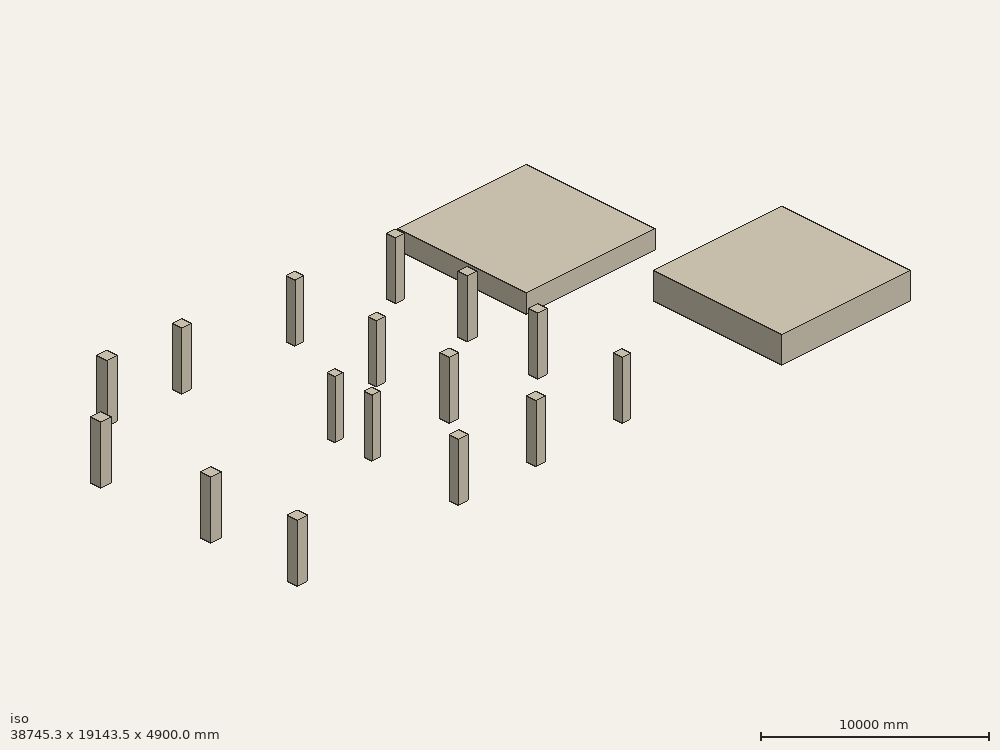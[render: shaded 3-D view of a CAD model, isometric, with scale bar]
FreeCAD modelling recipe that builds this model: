
FCSTD DOCUMENT  (FreeCAD 0.19R24291 (Git))
Label: single_foundation
License: All rights reserved
LicenseURL: http://en.wikipedia.org/wiki/All_rights_reserved
objects: Part::Part2DObjectPython×68, Part::FeaturePython×55, App::FeaturePython×17, App::DocumentObjectGroup×5
note: 280 computed .brp shape members not serialized (recipe doc carries the construction recipe); baked Part::Feature solids carry a one-line shape summary decoded from their .brp

FEATURE [Part::Part2DObjectPython] Line006  label="C1_Story1_CenterLine"  # Draft 2D object (typed FeaturePython)
  Area = 0
  ChamferSize = 0
  Closed = false
  End = (17740,20340,3350)
  FilletRadius = 0
  Length = 3350
  MakeFace = true
  Points = (2) [(17740,20340,0),(17740,20340,3350)]
  Start = (17740,20340,0)
  Subdivisions = 0
FEATURE [Part::Part2DObjectPython] C5512C  # Draft 2D object (typed FeaturePython)
  Height = 550
  Width = 550
FEATURE [Part::FeaturePython] Structure  label="C1_Story1"  # Arch/BIM 24 (typed FeaturePython)
  AttacherType = Attacher::AttachEngine3D
  AttachmentOffset = pos=(0,0,0) rot=(0,0,1;1.5708rad)
  Base = -> C5512C
  FaceMaker = 0
  Height = 3350
  HorizontalArea = 302500
  IfcData = attributes={"GlobalId": {"name": "GlobalId", "type": "IfcGloballyUniqueId", "is_enum": false, "enum_values": []}, "Description": {"... (+438 chars omitted),+1 more (map truncated)
  IfcType = 24
  Length = 0
  MapMode = 7
  MoveBase = false
  MoveWithHost = false
  Nodes = (2) [(17740,20340,0),(17740,20340,3350)]
  NodesOffset = 0
  Normal = (0,0,0)
  PerimeterLength = 2200
  Placement = pos=(17740,20340,0) rot=(0,0,1;1.5708rad)
  PredefinedType = 0
  Support = -> [Line006]
  VerticalArea = 7.37e+06
  Width = 200
  combos_load = Combo1 Max=2929.3594, 27006.37, 14808.13,Combo10 Max=2608.538, -98112.68, -391082.9,Combo11 Max=2657.75, -72288.26, -345375.92,+37 more (map truncated)
FEATURE [Part::Part2DObjectPython] Line007  label="C2_Story1_CenterLine"  # Draft 2D object (typed FeaturePython)
  Area = 0
  ChamferSize = 0
  Closed = false
  End = (23500,19838.5,3350)
  FilletRadius = 0
  Length = 3350
  MakeFace = true
  Points = (2) [(23500,19838.5,0),(23500,19838.5,3350)]
  Start = (23500,19838.5,0)
  Subdivisions = 0
FEATURE [Part::FeaturePython] Structure001  label="C2_Story1"  # Arch/BIM 24 (typed FeaturePython)
  AttacherType = Attacher::AttachEngine3D
  AttachmentOffset = pos=(0,0,0) rot=(0,0,1;1.5708rad)
  Base = -> C5512C
  FaceMaker = 0
  Height = 3350
  HorizontalArea = 302500
  IfcData = attributes={"GlobalId": {"name": "GlobalId", "type": "IfcGloballyUniqueId", "is_enum": false, "enum_values": []}, "Description": {"... (+438 chars omitted),+1 more (map truncated)
  IfcType = 24
  Length = 0
  MapMode = 7
  MoveBase = false
  MoveWithHost = false
  Nodes = (2) [(23500,19838.5,0),(23500,19838.5,3350)]
  NodesOffset = 0
  Normal = (0,0,0)
  PerimeterLength = 2200
  Placement = pos=(23500,19838.5,0) rot=(0,0,1;1.5708rad)
  PredefinedType = 0
  Support = -> [Line007]
  VerticalArea = 7.37e+06
  Width = 200
  combos_load = Combo1 Max=1754.8461, 12356.17, -26849.18,Combo10 Max=2143.525, -139905.36, -387343.42,Combo11 Max=2175.8338, -83310.12, -350318.73,+37 more (map truncated)
FEATURE [Part::Part2DObjectPython] Line008  label="C17_Story1_CenterLine"  # Draft 2D object (typed FeaturePython)
  Area = 0
  ChamferSize = 0
  Closed = false
  End = (23370,15250,3350)
  FilletRadius = 0
  Length = 3350
  MakeFace = true
  Points = (2) [(23370,15250,0),(23370,15250,3350)]
  Start = (23370,15250,0)
  Subdivisions = 0
FEATURE [Part::Part2DObjectPython] C6012AC  # Draft 2D object (typed FeaturePython)
  Height = 600
  Width = 600
FEATURE [Part::FeaturePython] Structure002  label="C17_Story1"  # Arch/BIM 24 (typed FeaturePython)
  AttacherType = Attacher::AttachEngine3D
  AttachmentOffset = pos=(0,0,0) rot=(0,0,1;1.5708rad)
  Base = -> C6012AC
  FaceMaker = 0
  Height = 3350
  HorizontalArea = 360000
  IfcData = attributes={"GlobalId": {"name": "GlobalId", "type": "IfcGloballyUniqueId", "is_enum": false, "enum_values": []}, "Description": {"... (+438 chars omitted),+1 more (map truncated)
  IfcType = 24
  Length = 0
  MapMode = 7
  MoveBase = false
  MoveWithHost = false
  Nodes = (2) [(23370,15250,0),(23370,15250,3350)]
  NodesOffset = 0
  Normal = (0,0,0)
  PerimeterLength = 2400
  Placement = pos=(23370,15250,0) rot=(0,0,1;1.5708rad)
  PredefinedType = 0
  Support = -> [Line008]
  VerticalArea = 8.04e+06
  Width = 200
  combos_load = Combo1 Max=1514.2218, -5536.02, -34563.49,Combo10 Max=1873.5598, -222983.25, -488160.13,Combo11 Max=1871.0673, -140666.82, -475481.05,+37 more (map truncated)
FEATURE [Part::Part2DObjectPython] Line009  label="C18_Story1_CenterLine"  # Draft 2D object (typed FeaturePython)
  Area = 0
  ChamferSize = 0
  Closed = false
  End = (23250,10750,3350)
  FilletRadius = 0
  Length = 3350
  MakeFace = true
  Points = (2) [(23250,10750,0),(23250,10750,3350)]
  Start = (23250,10750,0)
  Subdivisions = 0
FEATURE [Part::FeaturePython] Structure003  label="C18_Story1"  # Arch/BIM 24 (typed FeaturePython)
  AttacherType = Attacher::AttachEngine3D
  AttachmentOffset = pos=(0,0,0) rot=(0,0,1;1.5708rad)
  Base = -> C6012AC
  FaceMaker = 0
  Height = 3350
  HorizontalArea = 360000
  IfcData = attributes={"GlobalId": {"name": "GlobalId", "type": "IfcGloballyUniqueId", "is_enum": false, "enum_values": []}, "Description": {"... (+438 chars omitted),+1 more (map truncated)
  IfcType = 24
  Length = 0
  MapMode = 7
  MoveBase = false
  MoveWithHost = false
  Nodes = (2) [(23250,10750,0),(23250,10750,3350)]
  NodesOffset = 0
  Normal = (0,0,0)
  PerimeterLength = 2400
  Placement = pos=(23250,10750,0) rot=(0,0,1;1.5708rad)
  PredefinedType = 0
  Support = -> [Line009]
  VerticalArea = 8.04e+06
  Width = 200
  combos_load = Combo1 Max=1534.3408, 49.31, -39260.22,Combo10 Max=2051.3394, -213536.56, -457180.36,Combo11 Max=2057.4036, -133173.75, -478456.04,+37 more (map truncated)
FEATURE [Part::Part2DObjectPython] Line010  label="C5_Story1_CenterLine"  # Draft 2D object (typed FeaturePython)
  Area = 0
  ChamferSize = 0
  Closed = false
  End = (17740,5350,3350)
  FilletRadius = 0
  Length = 3350
  MakeFace = true
  Points = (2) [(17740,5350,0),(17740,5350,3350)]
  Start = (17740,5350,0)
  Subdivisions = 0
FEATURE [Part::FeaturePython] Structure004  label="C5_Story1"  # Arch/BIM 24 (typed FeaturePython)
  AttacherType = Attacher::AttachEngine3D
  AttachmentOffset = pos=(0,0,0) rot=(0,0,1;1.5708rad)
  Base = -> C6012AC
  FaceMaker = 0
  Height = 3350
  HorizontalArea = 360000
  IfcData = attributes={"GlobalId": {"name": "GlobalId", "type": "IfcGloballyUniqueId", "is_enum": false, "enum_values": []}, "Description": {"... (+438 chars omitted),+1 more (map truncated)
  IfcType = 24
  Length = 0
  MapMode = 7
  MoveBase = false
  MoveWithHost = false
  Nodes = (2) [(17740,5350,0),(17740,5350,3350)]
  NodesOffset = 0
  Normal = (0,0,0)
  PerimeterLength = 2400
  Placement = pos=(17740,5350,0) rot=(0,0,1;1.5708rad)
  PredefinedType = 0
  Support = -> [Line010]
  VerticalArea = 8.04e+06
  Width = 200
  combos_load = Combo1 Max=1623.3033, -947.79, -5177.17,Combo10 Max=1786.5067, -169313.57, -460450.33,Combo11 Max=1770.754, -135335.23, -531760.45,+37 more (map truncated)
FEATURE [Part::Part2DObjectPython] Line011  label="C6_Story1_CenterLine"  # Draft 2D object (typed FeaturePython)
  Area = 0
  ChamferSize = 0
  Closed = false
  End = (12940,5350,3350)
  FilletRadius = 0
  Length = 3350
  MakeFace = true
  Points = (2) [(12940,5350,0),(12940,5350,3350)]
  Start = (12940,5350,0)
  Subdivisions = 0
FEATURE [Part::FeaturePython] Structure005  label="C6_Story1"  # Arch/BIM 24 (typed FeaturePython)
  AttacherType = Attacher::AttachEngine3D
  AttachmentOffset = pos=(0,0,0) rot=(0,0,1;1.5708rad)
  Base = -> C6012AC
  FaceMaker = 0
  Height = 3350
  HorizontalArea = 360000
  IfcData = attributes={"GlobalId": {"name": "GlobalId", "type": "IfcGloballyUniqueId", "is_enum": false, "enum_values": []}, "Description": {"... (+438 chars omitted),+1 more (map truncated)
  IfcType = 24
  Length = 0
  MapMode = 7
  MoveBase = false
  MoveWithHost = false
  Nodes = (2) [(12940,5350,0),(12940,5350,3350)]
  NodesOffset = 0
  Normal = (0,0,0)
  PerimeterLength = 2400
  Placement = pos=(12940,5350,0) rot=(0,0,1;1.5708rad)
  PredefinedType = 0
  Support = -> [Line011]
  VerticalArea = 8.04e+06
  Width = 200
  combos_load = Combo1 Max=2458.9073, 10889.53, -106700.8,Combo10 Max=1939.8727, -132976.26, -554878.34,Combo11 Max=1860.3718, -132910.34, -622641.45,+37 more (map truncated)
FEATURE [Part::Part2DObjectPython] Line012  label="C19_Story1_CenterLine"  # Draft 2D object (typed FeaturePython)
  Area = 0
  ChamferSize = 0
  Closed = false
  End = (23100,5350,3350)
  FilletRadius = 0
  Length = 3350
  MakeFace = true
  Points = (2) [(23100,5350,0),(23100,5350,3350)]
  Start = (23100,5350,0)
  Subdivisions = 0
FEATURE [Part::Part2DObjectPython] C5512AC  # Draft 2D object (typed FeaturePython)
  Height = 550
  Width = 550
FEATURE [Part::FeaturePython] Structure006  label="C19_Story1"  # Arch/BIM 24 (typed FeaturePython)
  AttacherType = Attacher::AttachEngine3D
  AttachmentOffset = pos=(0,0,0) rot=(0,0,1;1.5708rad)
  Base = -> C5512AC
  FaceMaker = 0
  Height = 3350
  HorizontalArea = 302500
  IfcData = attributes={"GlobalId": {"name": "GlobalId", "type": "IfcGloballyUniqueId", "is_enum": false, "enum_values": []}, "Description": {"... (+438 chars omitted),+1 more (map truncated)
  IfcType = 24
  Length = 0
  MapMode = 7
  MoveBase = false
  MoveWithHost = false
  Nodes = (2) [(23100,5350,0),(23100,5350,3350)]
  NodesOffset = 0
  Normal = (0,0,0)
  PerimeterLength = 2200
  Placement = pos=(23100,5350,0) rot=(0,0,1;1.5708rad)
  PredefinedType = 0
  Support = -> [Line012]
  VerticalArea = 7.37e+06
  Width = 200
  combos_load = Combo1 Max=1051.5097, -14568.81, -35137.32,Combo10 Max=1680.8499, -155391.05, -323776.55,Combo11 Max=1698.4736, -101933.47, -370507.25,+37 more (map truncated)
FEATURE [Part::Part2DObjectPython] Line013  label="C8_Story1_CenterLine"  # Draft 2D object (typed FeaturePython)
  Area = 0
  ChamferSize = 0
  Closed = false
  End = (11240,20890,3350)
  FilletRadius = 0
  Length = 3350
  MakeFace = true
  Points = (2) [(11240,20890,0),(11240,20890,3350)]
  Start = (11240,20890,0)
  Subdivisions = 0
FEATURE [Part::Part2DObjectPython] C6012C  # Draft 2D object (typed FeaturePython)
  Height = 600
  Width = 600
FEATURE [Part::FeaturePython] Structure007  label="C8_Story1"  # Arch/BIM 24 (typed FeaturePython)
  AttacherType = Attacher::AttachEngine3D
  AttachmentOffset = pos=(0,0,0) rot=(0,0,1;1.5708rad)
  Base = -> C6012C
  FaceMaker = 0
  Height = 3350
  HorizontalArea = 360000
  IfcData = attributes={"GlobalId": {"name": "GlobalId", "type": "IfcGloballyUniqueId", "is_enum": false, "enum_values": []}, "Description": {"... (+438 chars omitted),+1 more (map truncated)
  IfcType = 24
  Length = 0
  MapMode = 7
  MoveBase = false
  MoveWithHost = false
  Nodes = (2) [(11240,20890,0),(11240,20890,3350)]
  NodesOffset = 0
  Normal = (0,0,0)
  PerimeterLength = 2400
  Placement = pos=(11240,20890,0) rot=(0,0,1;1.5708rad)
  PredefinedType = 0
  Support = -> [Line013]
  VerticalArea = 8.04e+06
  Width = 200
  combos_load = Combo1 Max=3176.7816, 67519.66, -1586.57,Combo10 Max=3690.7518, -72646.95, -573333.56,Combo11 Max=3628.5505, -82554.37, -507645.57,+37 more (map truncated)
FEATURE [Part::Part2DObjectPython] Line014  label="C9_Story1_CenterLine"  # Draft 2D object (typed FeaturePython)
  Area = 0
  ChamferSize = 0
  Closed = false
  End = (6930,21230,3350)
  FilletRadius = 0
  Length = 3350
  MakeFace = true
  Points = (2) [(6930,21230,0),(6930,21230,3350)]
  Start = (6930,21230,0)
  Subdivisions = 0
FEATURE [Part::Part2DObjectPython] C6516AC  # Draft 2D object (typed FeaturePython)
  Height = 650
  Width = 650
FEATURE [Part::FeaturePython] Structure008  label="C9_Story1"  # Arch/BIM 24 (typed FeaturePython)
  AttacherType = Attacher::AttachEngine3D
  AttachmentOffset = pos=(0,0,0) rot=(0,0,1;1.5708rad)
  Base = -> C6516AC
  FaceMaker = 0
  Height = 3350
  HorizontalArea = 422500
  IfcData = attributes={"GlobalId": {"name": "GlobalId", "type": "IfcGloballyUniqueId", "is_enum": false, "enum_values": []}, "Description": {"... (+438 chars omitted),+1 more (map truncated)
  IfcType = 24
  Length = 0
  MapMode = 7
  MoveBase = false
  MoveWithHost = false
  Nodes = (2) [(6930,21230,0),(6930,21230,3350)]
  NodesOffset = 0
  Normal = (0,0,0)
  PerimeterLength = 2600
  Placement = pos=(6930,21230,0) rot=(0,0,1;1.5708rad)
  PredefinedType = 0
  Support = -> [Line014]
  VerticalArea = 8.71e+06
  Width = 200
  combos_load = Combo1 Max=3178.5002, 13656.36, 31223.41,Combo10 Max=2579.0077, -108238.08, -657320.49,Combo11 Max=2529.7417, -170319.15, -568803.46,+37 more (map truncated)
FEATURE [Part::Part2DObjectPython] Line015  label="C10_Story1_CenterLine"  # Draft 2D object (typed FeaturePython)
  Area = 0
  ChamferSize = 0
  Closed = false
  End = (2900,17580,3350)
  FilletRadius = 0
  Length = 3350
  MakeFace = true
  Points = (2) [(2900,17580,0),(2900,17580,3350)]
  Start = (2900,17580,0)
  Subdivisions = 0
FEATURE [Part::FeaturePython] Structure009  label="C10_Story1"  # Arch/BIM 24 (typed FeaturePython)
  AttacherType = Attacher::AttachEngine3D
  AttachmentOffset = pos=(0,0,0) rot=(0,0,1;1.5708rad)
  Base = -> C6516AC
  FaceMaker = 0
  Height = 3350
  HorizontalArea = 422500
  IfcData = attributes={"GlobalId": {"name": "GlobalId", "type": "IfcGloballyUniqueId", "is_enum": false, "enum_values": []}, "Description": {"... (+438 chars omitted),+1 more (map truncated)
  IfcType = 24
  Length = 0
  MapMode = 7
  MoveBase = false
  MoveWithHost = false
  Nodes = (2) [(2900,17580,0),(2900,17580,3350)]
  NodesOffset = 0
  Normal = (0,0,0)
  PerimeterLength = 2600
  Placement = pos=(2900,17580,0) rot=(0,0,1;1.5708rad)
  PredefinedType = 0
  Support = -> [Line015]
  VerticalArea = 8.71e+06
  Width = 200
  combos_load = Combo1 Max=4513.1788, 66434.1, 128004.31,Combo10 Max=3493.9652, -29609.04, -415032.95,Combo11 Max=3559.9915, -136385.01, -369140.23,+37 more (map truncated)
FEATURE [Part::Part2DObjectPython] Line016  label="C16_Story1_CenterLine"  # Draft 2D object (typed FeaturePython)
  Area = 0
  ChamferSize = 0
  Closed = false
  End = (2900,5350,3350)
  FilletRadius = 0
  Length = 3350
  MakeFace = true
  Points = (2) [(2900,5350,0),(2900,5350,3350)]
  Start = (2900,5350,0)
  Subdivisions = 0
FEATURE [Part::Part2DObjectPython] C6516A  # Draft 2D object (typed FeaturePython)
  Height = 650
  Width = 650
FEATURE [Part::FeaturePython] Structure010  label="C16_Story1"  # Arch/BIM 24 (typed FeaturePython)
  AttacherType = Attacher::AttachEngine3D
  AttachmentOffset = pos=(0,0,0) rot=(0,0,1;1.5708rad)
  Base = -> C6516A
  FaceMaker = 0
  Height = 3350
  HorizontalArea = 422500
  IfcData = attributes={"GlobalId": {"name": "GlobalId", "type": "IfcGloballyUniqueId", "is_enum": false, "enum_values": []}, "Description": {"... (+438 chars omitted),+1 more (map truncated)
  IfcType = 24
  Length = 0
  MapMode = 7
  MoveBase = false
  MoveWithHost = false
  Nodes = (2) [(2900,5350,0),(2900,5350,3350)]
  NodesOffset = 0
  Normal = (0,0,0)
  PerimeterLength = 2600
  Placement = pos=(2900,5350,0) rot=(0,0,1;1.5708rad)
  PredefinedType = 0
  Support = -> [Line016]
  VerticalArea = 8.71e+06
  Width = 200
  combos_load = Combo1 Max=2178.0668, -11443.95, 110544.97,Combo10 Max=2207.6537, -146873.33, -349025.65,Combo11 Max=2312.863, -249404.95, -427796.67,+37 more (map truncated)
FEATURE [Part::Part2DObjectPython] Line017  label="C12_Story1_CenterLine"  # Draft 2D object (typed FeaturePython)
  Area = 0
  ChamferSize = 0
  Closed = false
  End = (17740,10750,3350)
  FilletRadius = 0
  Length = 3350
  MakeFace = true
  Points = (2) [(17740,10750,0),(17740,10750,3350)]
  Start = (17740,10750,0)
  Subdivisions = 0
FEATURE [Part::FeaturePython] Structure011  label="C12_Story1"  # Arch/BIM 24 (typed FeaturePython)
  AttacherType = Attacher::AttachEngine3D
  AttachmentOffset = pos=(0,0,0) rot=(0,0,1;1.5708rad)
  Base = -> C6012C
  FaceMaker = 0
  Height = 3350
  HorizontalArea = 360000
  IfcData = attributes={"GlobalId": {"name": "GlobalId", "type": "IfcGloballyUniqueId", "is_enum": false, "enum_values": []}, "Description": {"... (+438 chars omitted),+1 more (map truncated)
  IfcType = 24
  Length = 0
  MapMode = 7
  MoveBase = false
  MoveWithHost = false
  Nodes = (2) [(17740,10750,0),(17740,10750,3350)]
  NodesOffset = 0
  Normal = (0,0,0)
  PerimeterLength = 2400
  Placement = pos=(17740,10750,0) rot=(0,0,1;1.5708rad)
  PredefinedType = 0
  Support = -> [Line017]
  VerticalArea = 8.04e+06
  Width = 200
  combos_load = Combo1 Max=2372.5516, -20700, 4401.45,Combo10 Max=2415.4815, -204900.61, -476224.38,Combo11 Max=2407.8904, -168225.73, -499976.16,+37 more (map truncated)
FEATURE [Part::Part2DObjectPython] Line018  label="C13_Story1_CenterLine"  # Draft 2D object (typed FeaturePython)
  Area = 0
  ChamferSize = 0
  Closed = false
  End = (17740,15250,3350)
  FilletRadius = 0
  Length = 3350
  MakeFace = true
  Points = (2) [(17740,15250,0),(17740,15250,3350)]
  Start = (17740,15250,0)
  Subdivisions = 0
FEATURE [Part::FeaturePython] Structure012  label="C13_Story1"  # Arch/BIM 24 (typed FeaturePython)
  AttacherType = Attacher::AttachEngine3D
  AttachmentOffset = pos=(0,0,0) rot=(0,0,1;1.5708rad)
  Base = -> C5512C
  FaceMaker = 0
  Height = 3350
  HorizontalArea = 302500
  IfcData = attributes={"GlobalId": {"name": "GlobalId", "type": "IfcGloballyUniqueId", "is_enum": false, "enum_values": []}, "Description": {"... (+438 chars omitted),+1 more (map truncated)
  IfcType = 24
  Length = 0
  MapMode = 7
  MoveBase = false
  MoveWithHost = false
  Nodes = (2) [(17740,15250,0),(17740,15250,3350)]
  NodesOffset = 0
  Normal = (0,0,0)
  PerimeterLength = 2200
  Placement = pos=(17740,15250,0) rot=(0,0,1;1.5708rad)
  PredefinedType = 0
  Support = -> [Line018]
  VerticalArea = 7.37e+06
  Width = 200
  combos_load = Combo1 Max=2562.7432, -8357.02, -515.48,Combo10 Max=2113.2435, -155815.97, -358125.31,Combo11 Max=2129.9271, -128933.56, -347442.14,+37 more (map truncated)
FEATURE [Part::Part2DObjectPython] Line019  label="C14_Story1_CenterLine"  # Draft 2D object (typed FeaturePython)
  Area = 0
  ChamferSize = 0
  Closed = false
  End = (12940,10750,3350)
  FilletRadius = 0
  Length = 3350
  MakeFace = true
  Points = (2) [(12940,10750,0),(12940,10750,3350)]
  Start = (12940,10750,0)
  Subdivisions = 0
FEATURE [Part::Part2DObjectPython] C5012AC  # Draft 2D object (typed FeaturePython)
  Height = 500
  Width = 500
FEATURE [Part::FeaturePython] Structure013  label="C14_Story1"  # Arch/BIM 24 (typed FeaturePython)
  AttacherType = Attacher::AttachEngine3D
  AttachmentOffset = pos=(0,0,0) rot=(0,0,1;3.14159rad)
  Base = -> C5012AC
  FaceMaker = 0
  Height = 3350
  HorizontalArea = 250000
  IfcData = attributes={"GlobalId": {"name": "GlobalId", "type": "IfcGloballyUniqueId", "is_enum": false, "enum_values": []}, "Description": {"... (+438 chars omitted),+1 more (map truncated)
  IfcType = 24
  Length = 0
  MapMode = 7
  MoveBase = false
  MoveWithHost = false
  Nodes = (2) [(12940,10750,0),(12940,10750,3350)]
  NodesOffset = 0
  Normal = (0,0,0)
  PerimeterLength = 2000
  Placement = pos=(12940,10750,0) rot=(0,0,1;3.14159rad)
  PredefinedType = 0
  Support = -> [Line019]
  VerticalArea = 6.7e+06
  Width = 200
  combos_load = Combo1 Max=2582.1087, 172.69, -72462.15,Combo10 Max=2432.6339, -96294.19, -372624.2,Combo11 Max=2403.0715, -96603.51, -385451.48,+37 more (map truncated)
FEATURE [Part::Part2DObjectPython] Line020  label="C15_Story1_CenterLine"  # Draft 2D object (typed FeaturePython)
  Area = 0
  ChamferSize = 0
  Closed = false
  End = (12940,13050,3350)
  FilletRadius = 0
  Length = 3350
  MakeFace = true
  Points = (2) [(12940,13050,0),(12940,13050,3350)]
  Start = (12940,13050,0)
  Subdivisions = 0
FEATURE [Part::Part2DObjectPython] C5016A  # Draft 2D object (typed FeaturePython)
  Height = 500
  Width = 500
FEATURE [Part::FeaturePython] Structure014  label="C15_Story1"  # Arch/BIM 24 (typed FeaturePython)
  AttacherType = Attacher::AttachEngine3D
  AttachmentOffset = pos=(0,0,0) rot=(0,0,1;3.14159rad)
  Base = -> C5016A
  FaceMaker = 0
  Height = 3350
  HorizontalArea = 250000
  IfcData = attributes={"GlobalId": {"name": "GlobalId", "type": "IfcGloballyUniqueId", "is_enum": false, "enum_values": []}, "Description": {"... (+438 chars omitted),+1 more (map truncated)
  IfcType = 24
  Length = 0
  MapMode = 7
  MoveBase = false
  MoveWithHost = false
  Nodes = (2) [(12940,13050,0),(12940,13050,3350)]
  NodesOffset = 0
  Normal = (0,0,0)
  PerimeterLength = 2000
  Placement = pos=(12940,13050,0) rot=(0,0,1;3.14159rad)
  PredefinedType = 0
  Support = -> [Line020]
  VerticalArea = 6.7e+06
  Width = 200
  combos_load = Combo1 Max=3210.485, -73329.89, -94104.41,Combo10 Max=2840.0423, -210175.6, -361309.23,Combo11 Max=2844.4131, -210015.24, -363099.71,+37 more (map truncated)
FEATURE [Part::Part2DObjectPython] Line021  # Draft 2D object (typed FeaturePython)
  Area = 0
  ChamferSize = 0
  Closed = false
  End = (11240,20890,0)
  FilletRadius = 0
  Length = 4323.39
  MakeFace = true
  Points = (2) [(6930,21230,0),(11240,20890,0)]
  Start = (6930,21230,0)
  Subdivisions = 0
  type = Beam
FEATURE [Part::Part2DObjectPython] Line022  # Draft 2D object (typed FeaturePython)
  Area = 0
  ChamferSize = 0
  Closed = false
  End = (17740,20340,0)
  FilletRadius = 0
  Length = 6523.23
  MakeFace = true
  Points = (2) [(11240,20890,0),(17740,20340,0)]
  Start = (11240,20890,0)
  Subdivisions = 0
  type = Beam
FEATURE [Part::Part2DObjectPython] Line023  # Draft 2D object (typed FeaturePython)
  Area = 0
  ChamferSize = 0
  Closed = false
  End = (23500,19838.5,0)
  FilletRadius = 0
  Length = 5781.79
  MakeFace = true
  Points = (2) [(17740,20340,0),(23500,19838.5,0)]
  Start = (17740,20340,0)
  Subdivisions = 0
  type = Beam
FEATURE [Part::Part2DObjectPython] Line024  # Draft 2D object (typed FeaturePython)
  Area = 0
  ChamferSize = 0
  Closed = false
  End = (23500,19838.5,0)
  FilletRadius = 0
  Length = 4590.3
  MakeFace = true
  Points = (2) [(23370,15250,0),(23500,19838.5,0)]
  Start = (23370,15250,0)
  Subdivisions = 0
  type = Beam
FEATURE [Part::Part2DObjectPython] Line025  # Draft 2D object (typed FeaturePython)
  Area = 0
  ChamferSize = 0
  Closed = false
  End = (23370,15250,0)
  FilletRadius = 0
  Length = 4501.6
  MakeFace = true
  Points = (2) [(23250,10750,0),(23370,15250,0)]
  Start = (23250,10750,0)
  Subdivisions = 0
  type = Beam
FEATURE [Part::Part2DObjectPython] Line026  # Draft 2D object (typed FeaturePython)
  Area = 0
  ChamferSize = 0
  Closed = false
  End = (23100,5350,0)
  FilletRadius = 0
  Length = 5360
  MakeFace = true
  Points = (2) [(17740,5350,0),(23100,5350,0)]
  Start = (17740,5350,0)
  Subdivisions = 0
  type = Beam
FEATURE [Part::Part2DObjectPython] Line027  # Draft 2D object (typed FeaturePython)
  Area = 0
  ChamferSize = 0
  Closed = false
  End = (17740,5350,0)
  FilletRadius = 0
  Length = 4800
  MakeFace = true
  Points = (2) [(12940,5350,0),(17740,5350,0)]
  Start = (12940,5350,0)
  Subdivisions = 0
  type = Beam
FEATURE [Part::Part2DObjectPython] Line028  # Draft 2D object (typed FeaturePython)
  Area = 0
  ChamferSize = 0
  Closed = false
  End = (12940,5350,0)
  FilletRadius = 0
  Length = 10040
  MakeFace = true
  Points = (2) [(2900,5350,0),(12940,5350,0)]
  Start = (2900,5350,0)
  Subdivisions = 0
  type = Beam
FEATURE [Part::Part2DObjectPython] Line029  # Draft 2D object (typed FeaturePython)
  Area = 0
  ChamferSize = 0
  Closed = false
  End = (2900,10750,0)
  FilletRadius = 0
  Length = 5400
  MakeFace = true
  Points = (2) [(2900,5350,0),(2900,10750,0)]
  Start = (2900,5350,0)
  Subdivisions = 0
  type = Beam
FEATURE [Part::Part2DObjectPython] Line030  # Draft 2D object (typed FeaturePython)
  Area = 0
  ChamferSize = 0
  Closed = false
  End = (2900,17580,0)
  FilletRadius = 0
  Length = 6830
  MakeFace = true
  Points = (2) [(2900,10750,0),(2900,17580,0)]
  Start = (2900,10750,0)
  Subdivisions = 0
  type = Beam
FEATURE [Part::Part2DObjectPython] Line031  # Draft 2D object (typed FeaturePython)
  Area = 0
  ChamferSize = 0
  Closed = false
  End = (6930,21230,0)
  FilletRadius = 0
  Length = 5437.22
  MakeFace = true
  Points = (2) [(2900,17580,0),(6930,21230,0)]
  Start = (2900,17580,0)
  Subdivisions = 0
  type = Beam
FEATURE [Part::Part2DObjectPython] Line032  # Draft 2D object (typed FeaturePython)
  Area = 0
  ChamferSize = 0
  Closed = false
  End = (17740,10750,0)
  FilletRadius = 0
  Length = 5400
  MakeFace = true
  Points = (2) [(17740,5350,0),(17740,10750,0)]
  Start = (17740,5350,0)
  Subdivisions = 0
  type = Beam
FEATURE [Part::Part2DObjectPython] Line033  # Draft 2D object (typed FeaturePython)
  Area = 0
  ChamferSize = 0
  Closed = false
  End = (17740,15250,0)
  FilletRadius = 0
  Length = 4500
  MakeFace = true
  Points = (2) [(17740,10750,0),(17740,15250,0)]
  Start = (17740,10750,0)
  Subdivisions = 0
  type = Beam
FEATURE [Part::Part2DObjectPython] Line034  # Draft 2D object (typed FeaturePython)
  Area = 0
  ChamferSize = 0
  Closed = false
  End = (12940,10750,0)
  FilletRadius = 0
  Length = 5400
  MakeFace = true
  Points = (2) [(12940,5350,0),(12940,10750,0)]
  Start = (12940,5350,0)
  Subdivisions = 0
  type = Beam
FEATURE [Part::Part2DObjectPython] Line035  # Draft 2D object (typed FeaturePython)
  Area = 0
  ChamferSize = 0
  Closed = false
  End = (12940,13050,0)
  FilletRadius = 0
  Length = 2300
  MakeFace = true
  Points = (2) [(12940,10750,0),(12940,13050,0)]
  Start = (12940,10750,0)
  Subdivisions = 0
  type = Beam
FEATURE [Part::Part2DObjectPython] Line036  # Draft 2D object (typed FeaturePython)
  Area = 0
  ChamferSize = 0
  Closed = false
  End = (12940,13050,0)
  FilletRadius = 0
  Length = 8022.19
  MakeFace = true
  Points = (2) [(11240,20890,0),(12940,13050,0)]
  Start = (11240,20890,0)
  Subdivisions = 0
  type = Beam
FEATURE [Part::Part2DObjectPython] Line037  # Draft 2D object (typed FeaturePython)
  Area = 0
  ChamferSize = 0
  Closed = false
  End = (23250,10750,0)
  FilletRadius = 0
  Length = 5510
  MakeFace = true
  Points = (2) [(17740,10750,0),(23250,10750,0)]
  Start = (17740,10750,0)
  Subdivisions = 0
  type = Beam
FEATURE [Part::Part2DObjectPython] Line038  # Draft 2D object (typed FeaturePython)
  Area = 0
  ChamferSize = 0
  Closed = false
  End = (17740,10750,0)
  FilletRadius = 0
  Length = 4800
  MakeFace = true
  Points = (2) [(12940,10750,0),(17740,10750,0)]
  Start = (12940,10750,0)
  Subdivisions = 0
  type = Beam
FEATURE [Part::Part2DObjectPython] Line039  # Draft 2D object (typed FeaturePython)
  Area = 0
  ChamferSize = 0
  Closed = false
  End = (12940,10750,0)
  FilletRadius = 0
  Length = 10040
  MakeFace = true
  Points = (2) [(2900,10750,0),(12940,10750,0)]
  Start = (2900,10750,0)
  Subdivisions = 0
  type = Beam
FEATURE [Part::Part2DObjectPython] Line040  # Draft 2D object (typed FeaturePython)
  Area = 0
  ChamferSize = 0
  Closed = false
  End = (12940,13050,0)
  FilletRadius = 0
  Length = 11014.6
  MakeFace = true
  Points = (2) [(2900,17580,0),(12940,13050,0)]
  Start = (2900,17580,0)
  Subdivisions = 0
  type = Beam
FEATURE [Part::Part2DObjectPython] Line041  # Draft 2D object (typed FeaturePython)
  Area = 0
  ChamferSize = 0
  Closed = false
  End = (23370,15250,0)
  FilletRadius = 0
  Length = 5630
  MakeFace = true
  Points = (2) [(17740,15250,0),(23370,15250,0)]
  Start = (17740,15250,0)
  Subdivisions = 0
  type = Beam
FEATURE [Part::Part2DObjectPython] Line042  label="C11_Story1_CenterLine"  # Draft 2D object (typed FeaturePython)
  Area = 0
  ChamferSize = 0
  Closed = false
  End = (2900,10750,3350)
  FilletRadius = 0
  Length = 3350
  MakeFace = true
  Points = (2) [(2900,10750,0),(2900,10750,3350)]
  Start = (2900,10750,0)
  Subdivisions = 0
FEATURE [Part::FeaturePython] Structure015  label="C11_Story1"  # Arch/BIM 24 (typed FeaturePython)
  AttacherType = Attacher::AttachEngine3D
  AttachmentOffset = pos=(0,0,0) rot=(0,0,1;1.5708rad)
  Base = -> C6516A
  FaceMaker = 0
  Height = 3350
  HorizontalArea = 422500
  IfcData = attributes={"GlobalId": {"name": "GlobalId", "type": "IfcGloballyUniqueId", "is_enum": false, "enum_values": []}, "Description": {"... (+438 chars omitted),+1 more (map truncated)
  IfcType = 24
  Length = 0
  MapMode = 7
  MoveBase = false
  MoveWithHost = false
  Nodes = (2) [(2900,10750,0),(2900,10750,3350)]
  NodesOffset = 0
  Normal = (0,0,0)
  PerimeterLength = 2600
  Placement = pos=(2900,10750,0) rot=(0,0,1;1.5708rad)
  PredefinedType = 0
  Support = -> [Line042]
  VerticalArea = 8.71e+06
  Width = 200
  combos_load = Combo1 Max=3352.5419, -47728.92, 119986.56,Combo10 Max=3085.1187, -203250.05, -354468.47,Combo11 Max=3033.9869, -319766.11, -381702.35,+37 more (map truncated)
FEATURE [App::DocumentObjectGroup] Columns
  Group = -> [Structure,Structure001,Structure002,Structure003,Structure004,Structure005,Structure006,Structure007,Structure008,Structure009,Structure010,Structure011,Structure012,Structure013,Structure014,Structure015]
FEATURE [Part::Part2DObjectPython] Line043  # Draft 2D object (typed FeaturePython)
  Area = 0
  ChamferSize = 0
  Closed = false
  End = (17740,13050,0)
  FilletRadius = 0
  Length = 4800
  MakeFace = true
  Points = (2) [(12940,13050,0),(17740,13050,0)]
  Start = (12940,13050,0)
  Subdivisions = 0
  type = Beam
FEATURE [Part::Part2DObjectPython] Line047  # Draft 2D object (typed FeaturePython)
  Area = 0
  ChamferSize = 0
  Closed = false
  End = (17740,20340,0)
  FilletRadius = 0
  Length = 5090
  MakeFace = true
  Points = (2) [(17740,15250,0),(17740,20340,0)]
  Start = (17740,15250,0)
  Subdivisions = 0
  type = Beam
FEATURE [Part::Part2DObjectPython] Line048  # Draft 2D object (typed FeaturePython)
  Area = 0
  ChamferSize = 0
  Closed = false
  End = (23250,10750,0)
  FilletRadius = 0
  Length = 5402.08
  MakeFace = true
  Points = (2) [(23100,5350,0),(23250,10750,0)]
  Start = (23100,5350,0)
  Subdivisions = 0
  type = Beam
FEATURE [App::DocumentObjectGroup] Beams
  Group = -> [Line021,Line022,Line023,Line024,Line025,Line026,Line027,Line028,Line029,Line030,Line031,Line032,Line033,Line034,Line035,Line036,Line037,Line038,Line039,Line040,Line041,Line043,Line047,Line048]
FEATURE [App::FeaturePython] Safe  # WARN: FeaturePython — macro-defined, semantics opaque (R4)
  input = <path>
  input_str = <blob: 128872 chars omitted>
  output = <path>
FEATURE [Part::Part2DObjectPython] Wire  # Draft 2D object (typed FeaturePython)
  Area = 0
  ChamferSize = 0
  Closed = false
  End = (2900,17580,0)
  FilletRadius = 0
  Length = 12230
  MakeFace = false
  Points = (3) [(2900,5350,0),(2900,10750,0),(2900,17580,0)]
  Start = (2900,5350,0)
  Subdivisions = 0
FEATURE [Part::FeaturePython] BaseFoundation  # Arch/BIM 77 (typed FeaturePython)
  Base = -> Wire
  HorizontalArea = 0
  IfcData = attributes={"GlobalId": {"name": "GlobalId", "type": "IfcGloballyUniqueId", "is_enum": false, "enum_values": []}, "Description": {"... (+511 chars omitted),+1 more (map truncated)
  IfcType = 77
  MoveBase = false
  MoveWithHost = false
  PerimeterLength = 0
  PredefinedType = 0
  VerticalArea = 0
  align = 0
  design_type = 0
  fc = 25000
  final_wire_first_point = (0,0,0)
  final_wire_last_point = (0,0,0)
  height = 1000
  ks = 2
  layer = 1
  left_width = 500
  right_width = 500
  width = 1000
FEATURE [Part::Part2DObjectPython] Wire001  # Draft 2D object (typed FeaturePython)
  Area = 0
  ChamferSize = 0
  Closed = false
  End = (23100,5350,0)
  FilletRadius = 0
  Length = 20200
  MakeFace = false
  Points = (4) [(2900,5350,0),(12940,5350,0),(17740,5350,0),(23100,5350,0)]
  Start = (2900,5350,0)
  Subdivisions = 0
FEATURE [Part::FeaturePython] BaseFoundation001  # Arch/BIM 77 (typed FeaturePython)
  Base = -> Wire001
  HorizontalArea = 0
  IfcData = attributes={"GlobalId": {"name": "GlobalId", "type": "IfcGloballyUniqueId", "is_enum": false, "enum_values": []}, "Description": {"... (+511 chars omitted),+1 more (map truncated)
  IfcType = 77
  MoveBase = false
  MoveWithHost = false
  PerimeterLength = 0
  PredefinedType = 0
  VerticalArea = 0
  align = 0
  design_type = 0
  fc = 25000
  final_wire_first_point = (0,0,0)
  final_wire_last_point = (0,0,0)
  height = 1000
  ks = 2
  layer = 0
  left_width = 500
  right_width = 500
  width = 1000
FEATURE [Part::Part2DObjectPython] Wire002  # Draft 2D object (typed FeaturePython)
  Area = 0
  ChamferSize = 0
  Closed = false
  End = (23250,10750,0)
  FilletRadius = 0
  Length = 20350
  MakeFace = false
  Points = (4) [(2900,10750,0),(12940,10750,0),(17740,10750,0),(23250,10750,0)]
  Start = (2900,10750,0)
  Subdivisions = 0
FEATURE [Part::FeaturePython] BaseFoundation002  # Arch/BIM 77 (typed FeaturePython)
  Base = -> Wire002
  HorizontalArea = 0
  IfcData = attributes={"GlobalId": {"name": "GlobalId", "type": "IfcGloballyUniqueId", "is_enum": false, "enum_values": []}, "Description": {"... (+511 chars omitted),+1 more (map truncated)
  IfcType = 77
  MoveBase = false
  MoveWithHost = false
  PerimeterLength = 0
  PredefinedType = 0
  VerticalArea = 0
  align = 0
  design_type = 0
  fc = 25000
  final_wire_first_point = (0,0,0)
  final_wire_last_point = (0,0,0)
  height = 1000
  ks = 2
  layer = 0
  left_width = 500
  right_width = 500
  width = 1000
FEATURE [Part::Part2DObjectPython] Line  # Draft 2D object (typed FeaturePython)
  Area = 0
  ChamferSize = 0
  Closed = false
  End = (6930,21230,0)
  FilletRadius = 0
  Length = 5437.22
  MakeFace = false
  Points = (2) [(2900,17580,0),(6930,21230,0)]
  Start = (2900,17580,0)
  Subdivisions = 0
FEATURE [Part::FeaturePython] BaseFoundation003  # Arch/BIM 77 (typed FeaturePython)
  Base = -> Line
  HorizontalArea = 0
  IfcData = attributes={"GlobalId": {"name": "GlobalId", "type": "IfcGloballyUniqueId", "is_enum": false, "enum_values": []}, "Description": {"... (+511 chars omitted),+1 more (map truncated)
  IfcType = 77
  MoveBase = false
  MoveWithHost = false
  PerimeterLength = 0
  PredefinedType = 0
  VerticalArea = 0
  align = 0
  design_type = 0
  fc = 25000
  final_wire_first_point = (0,0,0)
  final_wire_last_point = (0,0,0)
  height = 1000
  ks = 2
  layer = 0
  left_width = 500
  right_width = 500
  width = 1000
FEATURE [Part::Part2DObjectPython] Wire003  # Draft 2D object (typed FeaturePython)
  Area = 0
  ChamferSize = 0
  Closed = false
  End = (17740,13050,0)
  FilletRadius = 0
  Length = 15814.6
  MakeFace = false
  Points = (3) [(2900,17580,0),(12940,13050,0),(17740,13050,0)]
  Start = (2900,17580,0)
  Subdivisions = 0
FEATURE [Part::FeaturePython] BaseFoundation004  # Arch/BIM 77 (typed FeaturePython)
  Base = -> Wire003
  HorizontalArea = 0
  IfcData = attributes={"GlobalId": {"name": "GlobalId", "type": "IfcGloballyUniqueId", "is_enum": false, "enum_values": []}, "Description": {"... (+511 chars omitted),+1 more (map truncated)
  IfcType = 77
  MoveBase = false
  MoveWithHost = false
  PerimeterLength = 0
  PredefinedType = 0
  VerticalArea = 0
  align = 0
  design_type = 0
  fc = 25000
  final_wire_first_point = (0,0,0)
  final_wire_last_point = (0,0,0)
  height = 1000
  ks = 2
  layer = 0
  left_width = 500
  right_width = 500
  width = 1000
FEATURE [Part::Part2DObjectPython] Wire004  # Draft 2D object (typed FeaturePython)
  Area = 0
  ChamferSize = 0
  Closed = false
  End = (23500,19838.5,0)
  FilletRadius = 0
  Length = 16628.4
  MakeFace = false
  Points = (4) [(6930,21230,0),(11240,20890,0),(17740,20340,0),(23500,19838.5,0)]
  Start = (6930,21230,0)
  Subdivisions = 0
FEATURE [Part::FeaturePython] BaseFoundation005  # Arch/BIM 77 (typed FeaturePython)
  Base = -> Wire004
  HorizontalArea = 0
  IfcData = attributes={"GlobalId": {"name": "GlobalId", "type": "IfcGloballyUniqueId", "is_enum": false, "enum_values": []}, "Description": {"... (+511 chars omitted),+1 more (map truncated)
  IfcType = 77
  MoveBase = false
  MoveWithHost = false
  PerimeterLength = 0
  PredefinedType = 0
  VerticalArea = 0
  align = 0
  design_type = 0
  fc = 25000
  final_wire_first_point = (0,0,0)
  final_wire_last_point = (0,0,0)
  height = 1000
  ks = 2
  layer = 0
  left_width = 500
  right_width = 500
  width = 1000
FEATURE [Part::Part2DObjectPython] Wire005  # Draft 2D object (typed FeaturePython)
  Area = 0
  ChamferSize = 0
  Closed = false
  End = (12940,5350,0)
  FilletRadius = 0
  Length = 15722.2
  MakeFace = false
  Points = (4) [(11240,20890,0),(12940,13050,0),(12940,10750,0),(12940,5350,0)]
  Start = (11240,20890,0)
  Subdivisions = 0
FEATURE [Part::FeaturePython] BaseFoundation006  # Arch/BIM 77 (typed FeaturePython)
  Base = -> Wire005
  HorizontalArea = 0
  IfcData = attributes={"GlobalId": {"name": "GlobalId", "type": "IfcGloballyUniqueId", "is_enum": false, "enum_values": []}, "Description": {"... (+511 chars omitted),+1 more (map truncated)
  IfcType = 77
  MoveBase = false
  MoveWithHost = false
  PerimeterLength = 0
  PredefinedType = 0
  VerticalArea = 0
  align = 0
  design_type = 0
  fc = 25000
  final_wire_first_point = (0,0,0)
  final_wire_last_point = (0,0,0)
  height = 1000
  ks = 2
  layer = 1
  left_width = 500
  right_width = 500
  width = 1000
FEATURE [Part::Part2DObjectPython] Wire006  # Draft 2D object (typed FeaturePython)
  Area = 0
  ChamferSize = 0
  Closed = false
  End = (17740,20340,0)
  FilletRadius = 0
  Length = 14990
  MakeFace = false
  Points = (4) [(17740,5350,0),(17740,10750,0),(17740,15250,0),(17740,20340,0)]
  Start = (17740,5350,0)
  Subdivisions = 0
FEATURE [Part::FeaturePython] BaseFoundation007  # Arch/BIM 77 (typed FeaturePython)
  Base = -> Wire006
  HorizontalArea = 0
  IfcData = attributes={"GlobalId": {"name": "GlobalId", "type": "IfcGloballyUniqueId", "is_enum": false, "enum_values": []}, "Description": {"... (+511 chars omitted),+1 more (map truncated)
  IfcType = 77
  MoveBase = false
  MoveWithHost = false
  PerimeterLength = 0
  PredefinedType = 0
  VerticalArea = 0
  align = 0
  design_type = 0
  fc = 25000
  final_wire_first_point = (0,0,0)
  final_wire_last_point = (0,0,0)
  height = 1000
  ks = 2
  layer = 1
  left_width = 500
  right_width = 500
  width = 1000
FEATURE [Part::Part2DObjectPython] Line049  # Draft 2D object (typed FeaturePython)
  Area = 0
  ChamferSize = 0
  Closed = false
  End = (23370,15250,0)
  FilletRadius = 0
  Length = 5630
  MakeFace = false
  Points = (2) [(17740,15250,0),(23370,15250,0)]
  Start = (17740,15250,0)
  Subdivisions = 0
FEATURE [Part::FeaturePython] BaseFoundation008  # Arch/BIM 77 (typed FeaturePython)
  Base = -> Line049
  HorizontalArea = 0
  IfcData = attributes={"GlobalId": {"name": "GlobalId", "type": "IfcGloballyUniqueId", "is_enum": false, "enum_values": []}, "Description": {"... (+511 chars omitted),+1 more (map truncated)
  IfcType = 77
  MoveBase = false
  MoveWithHost = false
  PerimeterLength = 0
  PredefinedType = 0
  VerticalArea = 0
  align = 0
  design_type = 0
  fc = 25000
  final_wire_first_point = (0,0,0)
  final_wire_last_point = (0,0,0)
  height = 1000
  ks = 2
  layer = 0
  left_width = 500
  right_width = 500
  width = 1000
FEATURE [Part::Part2DObjectPython] Wire007  # Draft 2D object (typed FeaturePython)
  Area = 0
  ChamferSize = 0
  Closed = false
  End = (23500,19838.5,0)
  FilletRadius = 0
  Length = 14494
  MakeFace = false
  Points = (4) [(23100,5350,0),(23250,10750,0),(23370,15250,0),(23500,19838.5,0)]
  Start = (23100,5350,0)
  Subdivisions = 0
FEATURE [Part::FeaturePython] BaseFoundation009  # Arch/BIM 77 (typed FeaturePython)
  Base = -> Wire007
  HorizontalArea = 0
  IfcData = attributes={"GlobalId": {"name": "GlobalId", "type": "IfcGloballyUniqueId", "is_enum": false, "enum_values": []}, "Description": {"... (+511 chars omitted),+1 more (map truncated)
  IfcType = 77
  MoveBase = false
  MoveWithHost = false
  PerimeterLength = 0
  PredefinedType = 0
  VerticalArea = 0
  align = 0
  design_type = 0
  fc = 25000
  final_wire_first_point = (0,0,0)
  final_wire_last_point = (0,0,0)
  height = 1000
  ks = 2
  layer = 1
  left_width = 500
  right_width = 500
  width = 1000
FEATURE [Part::FeaturePython] Foundation  # Arch/BIM 77 (typed FeaturePython)
  HorizontalArea = 0
  IfcType = 77
  MoveBase = false
  MoveWithHost = false
  PerimeterLength = 0
  VerticalArea = 0
  base_foundations = -> [BaseFoundation,BaseFoundation001,BaseFoundation002,BaseFoundation003,BaseFoundation004,BaseFoundation005,BaseFoundation006,BaseFoundation007,BaseFoundation008,BaseFoundation009]
  continuous_layer = 0
  cover = 75
  d = 775
  fc = 25000
  foundation_type = 0
  height = 850
  height_punch = 850
  ks = 2
  level = 0
  redraw = false
  split = true
  tolerance = 0
  volume = 115.321
FEATURE [Part::Part2DObjectPython] Line050  # Draft 2D object (typed FeaturePython)
  Area = 0
  ChamferSize = 0
  Closed = false
  End = (2900,18128.5,0)
  FilletRadius = 0
  Length = 13278.5
  MakeFace = false
  Points = (2) [(2900,4850,0),(2900,18128.5,0)]
  Start = (2900,4850,0)
  Subdivisions = 0
FEATURE [Part::FeaturePython] Strip  label="CSB1"  # Arch/BIM 0 (typed FeaturePython)
  Base = -> Line050
  HorizontalArea = 0
  IfcData = attributes={"GlobalId": {"name": "GlobalId", "type": "IfcGloballyUniqueId", "is_enum": false, "enum_values": []}, "Description": {"... (+538 chars omitted),+1 more (map truncated)
  IfcType = 0
  MoveBase = false
  MoveWithHost = false
  PerimeterLength = 0
  PredefinedType = 0
  VerticalArea = 0
  align = 0
  design_type = 0
  layer = 1
  left_width = 500
  right_width = 500
  width = 1000
FEATURE [Part::Part2DObjectPython] Line051  # Draft 2D object (typed FeaturePython)
  Area = 0
  ChamferSize = 0
  Closed = false
  End = (23600.2,5350,0)
  FilletRadius = 0
  Length = 21200.2
  MakeFace = false
  Points = (2) [(2400,5350,0),(23600.2,5350,0)]
  Start = (2400,5350,0)
  Subdivisions = 0
FEATURE [Part::FeaturePython] Strip001  label="CSA1"  # Arch/BIM 0 (typed FeaturePython)
  Base = -> Line051
  HorizontalArea = 0
  IfcData = attributes={"GlobalId": {"name": "GlobalId", "type": "IfcGloballyUniqueId", "is_enum": false, "enum_values": []}, "Description": {"... (+538 chars omitted),+1 more (map truncated)
  IfcType = 0
  MoveBase = false
  MoveWithHost = false
  PerimeterLength = 0
  PredefinedType = 0
  VerticalArea = 0
  align = 0
  design_type = 0
  layer = 0
  left_width = 500
  right_width = 500
  width = 1000
FEATURE [Part::Part2DObjectPython] Line052  # Draft 2D object (typed FeaturePython)
  Area = 0
  ChamferSize = 0
  Closed = false
  End = (23750.2,10750,0)
  FilletRadius = 0
  Length = 21350.2
  MakeFace = false
  Points = (2) [(2400,10750,0),(23750.2,10750,0)]
  Start = (2400,10750,0)
  Subdivisions = 0
FEATURE [Part::FeaturePython] Strip002  label="CSA2"  # Arch/BIM 0 (typed FeaturePython)
  Base = -> Line052
  HorizontalArea = 0
  IfcData = attributes={"GlobalId": {"name": "GlobalId", "type": "IfcGloballyUniqueId", "is_enum": false, "enum_values": []}, "Description": {"... (+538 chars omitted),+1 more (map truncated)
  IfcType = 0
  MoveBase = false
  MoveWithHost = false
  PerimeterLength = 0
  PredefinedType = 0
  VerticalArea = 0
  align = 0
  design_type = 0
  layer = 0
  left_width = 500
  right_width = 500
  width = 1000
FEATURE [Part::Part2DObjectPython] Line053  # Draft 2D object (typed FeaturePython)
  Area = 0
  ChamferSize = 0
  Closed = false
  End = (7439.4,21691.4,0)
  FilletRadius = 0
  Length = 6669.92
  MakeFace = false
  Points = (2) [(2495.74,17213.9,0),(7439.4,21691.4,0)]
  Start = (2495.74,17213.9,0)
  Subdivisions = 0
FEATURE [Part::FeaturePython] Strip003  label="CSA3"  # Arch/BIM 0 (typed FeaturePython)
  Base = -> Line053
  HorizontalArea = 0
  IfcData = attributes={"GlobalId": {"name": "GlobalId", "type": "IfcGloballyUniqueId", "is_enum": false, "enum_values": []}, "Description": {"... (+538 chars omitted),+1 more (map truncated)
  IfcType = 0
  MoveBase = false
  MoveWithHost = false
  PerimeterLength = 0
  PredefinedType = 0
  VerticalArea = 0
  align = 0
  design_type = 0
  layer = 0
  left_width = 500
  right_width = 500
  width = 1000
FEATURE [Part::Part2DObjectPython] Wire008  # Draft 2D object (typed FeaturePython)
  Area = 0
  ChamferSize = 0
  Closed = false
  End = (18240,13050,0)
  FilletRadius = 0
  Length = 16860.1
  MakeFace = false
  Points = (3) [(2402.84,17804.3,0),(12940,13050,0),(18240,13050,0)]
  Start = (2402.84,17804.3,0)
  Subdivisions = 0
FEATURE [Part::FeaturePython] Strip004  label="CSA4"  # Arch/BIM 0 (typed FeaturePython)
  Base = -> Wire008
  HorizontalArea = 0
  IfcData = attributes={"GlobalId": {"name": "GlobalId", "type": "IfcGloballyUniqueId", "is_enum": false, "enum_values": []}, "Description": {"... (+538 chars omitted),+1 more (map truncated)
  IfcType = 0
  MoveBase = false
  MoveWithHost = false
  PerimeterLength = 0
  PredefinedType = 0
  VerticalArea = 0
  align = 0
  design_type = 0
  layer = 0
  left_width = 500
  right_width = 500
  width = 1000
FEATURE [Part::Part2DObjectPython] Line054  # Draft 2D object (typed FeaturePython)
  Area = 0
  ChamferSize = 0
  Closed = false
  End = (23999,19795,0)
  FilletRadius = 0
  Length = 17816.5
  MakeFace = false
  Points = (2) [(6244.85,21284,0),(23999,19795,0)]
  Start = (6244.85,21284,0)
  Subdivisions = 0
FEATURE [Part::FeaturePython] Strip005  label="CSA5"  # Arch/BIM 0 (typed FeaturePython)
  Base = -> Line054
  HorizontalArea = 0
  IfcData = attributes={"GlobalId": {"name": "GlobalId", "type": "IfcGloballyUniqueId", "is_enum": false, "enum_values": []}, "Description": {"... (+538 chars omitted),+1 more (map truncated)
  IfcType = 0
  MoveBase = false
  MoveWithHost = false
  PerimeterLength = 0
  PredefinedType = 0
  VerticalArea = 0
  align = 0
  design_type = 0
  layer = 0
  left_width = 500
  right_width = 500
  width = 1000
FEATURE [Part::Part2DObjectPython] Wire009  # Draft 2D object (typed FeaturePython)
  Area = 0
  ChamferSize = 0
  Closed = false
  End = (12940,4850,0)
  FilletRadius = 0
  Length = 16744.3
  MakeFace = false
  Points = (3) [(11129.4,21400.3,0),(12940,13050,0),(12940,4850,0)]
  Start = (11129.4,21400.3,0)
  Subdivisions = 0
FEATURE [Part::FeaturePython] Strip006  label="CSB2"  # Arch/BIM 0 (typed FeaturePython)
  Base = -> Wire009
  HorizontalArea = 0
  IfcData = attributes={"GlobalId": {"name": "GlobalId", "type": "IfcGloballyUniqueId", "is_enum": false, "enum_values": []}, "Description": {"... (+538 chars omitted),+1 more (map truncated)
  IfcType = 0
  MoveBase = false
  MoveWithHost = false
  PerimeterLength = 0
  PredefinedType = 0
  VerticalArea = 0
  align = 0
  design_type = 0
  layer = 1
  left_width = 500
  right_width = 500
  width = 1000
FEATURE [Part::Part2DObjectPython] Line055  # Draft 2D object (typed FeaturePython)
  Area = 0
  ChamferSize = 0
  Closed = false
  End = (17740,20841.8,0)
  FilletRadius = 0
  Length = 15991.8
  MakeFace = false
  Points = (2) [(17740,4850,0),(17740,20841.8,0)]
  Start = (17740,4850,0)
  Subdivisions = 0
FEATURE [Part::FeaturePython] Strip007  label="CSB3"  # Arch/BIM 0 (typed FeaturePython)
  Base = -> Line055
  HorizontalArea = 0
  IfcData = attributes={"GlobalId": {"name": "GlobalId", "type": "IfcGloballyUniqueId", "is_enum": false, "enum_values": []}, "Description": {"... (+538 chars omitted),+1 more (map truncated)
  IfcType = 0
  MoveBase = false
  MoveWithHost = false
  PerimeterLength = 0
  PredefinedType = 0
  VerticalArea = 0
  align = 0
  design_type = 0
  layer = 1
  left_width = 500
  right_width = 500
  width = 1000
FEATURE [Part::Part2DObjectPython] Line056  # Draft 2D object (typed FeaturePython)
  Area = 0
  ChamferSize = 0
  Closed = false
  End = (23870.2,15250,0)
  FilletRadius = 0
  Length = 6630.2
  MakeFace = false
  Points = (2) [(17240,15250,0),(23870.2,15250,0)]
  Start = (17240,15250,0)
  Subdivisions = 0
FEATURE [Part::FeaturePython] Strip008  label="CSA6"  # Arch/BIM 0 (typed FeaturePython)
  Base = -> Line056
  HorizontalArea = 0
  IfcData = attributes={"GlobalId": {"name": "GlobalId", "type": "IfcGloballyUniqueId", "is_enum": false, "enum_values": []}, "Description": {"... (+538 chars omitted),+1 more (map truncated)
  IfcType = 0
  MoveBase = false
  MoveWithHost = false
  PerimeterLength = 0
  PredefinedType = 0
  VerticalArea = 0
  align = 0
  design_type = 0
  layer = 0
  left_width = 500
  right_width = 500
  width = 1000
FEATURE [App::DocumentObjectGroup] A_strips
  Group = -> [Strip001,Strip002,Strip003,Strip004,Strip005,Strip008]
FEATURE [Part::Part2DObjectPython] Line057  # Draft 2D object (typed FeaturePython)
  Area = 0
  ChamferSize = 0
  Closed = false
  End = (23514.2,20339.1,0)
  FilletRadius = 0
  Length = 15495
  MakeFace = false
  Points = (2) [(23086.1,4850,0),(23514.2,20339.1,0)]
  Start = (23086.1,4850,0)
  Subdivisions = 0
FEATURE [Part::FeaturePython] Strip009  label="CSB4"  # Arch/BIM 0 (typed FeaturePython)
  Base = -> Line057
  HorizontalArea = 0
  IfcData = attributes={"GlobalId": {"name": "GlobalId", "type": "IfcGloballyUniqueId", "is_enum": false, "enum_values": []}, "Description": {"... (+538 chars omitted),+1 more (map truncated)
  IfcType = 0
  MoveBase = false
  MoveWithHost = false
  PerimeterLength = 0
  PredefinedType = 0
  VerticalArea = 0
  align = 0
  design_type = 0
  layer = 1
  left_width = 500
  right_width = 500
  width = 1000
FEATURE [App::DocumentObjectGroup] B_strips
  Group = -> [Strip,Strip006,Strip007,Strip009]
FEATURE [App::FeaturePython] Text  # WARN: FeaturePython — macro-defined, semantics opaque (R4)
  Placement = pos=(17740,20897.8,3350) rot=(0,0,1;0rad)
  Text = Edge 3 | 1.74
FEATURE [Part::FeaturePython] Punch  # WARN: FeaturePython — macro-defined, semantics opaque (R4)
  Area = 2.3307e+06
  Av = 400
  Fys = 340000
  I22 = 4.39979e+11
  I23 = 2.26785e+11
  I33 = 7.86181e+11
  Location = 6
  Ratio = 1.74
  Use_Reinforcement = true
  Vc = 2.91338e+09
  Vs = 3.83012e+09
  Vu = 5.05762e+09
  alpha_s = 30
  angle = 0
  b0 = 3007.36
  bx = 550
  by = 550
  center_of_column = (17740,20340,0)
  center_of_load = (17740,20340,0)
  center_of_punch = (17740,20119.2,-387.5)
  column = -> Structure
  combos_ratio = Combo1=1.28,Combo10=0.99,Combo11=0.99,Combo12=1.63,Combo13=1.58,Combo14=1.42,Combo15=1.38,Combo16=1.60,Combo17=1.54,Combo18=1.74,Combo19=1.67,+30 more (map truncated)
  d = 775
  fc = 25000
  foundation = -> Foundation
  gamma_vx = 0.4
  gamma_vy = 0.4
  id = C1_Story1
  one_way_shear_capacity = 1.45669e+09
  s = 27.5187
  text = -> Text
  user_location = false
  vc = 1250
  x = 2105.24
FEATURE [App::FeaturePython] Text001  # WARN: FeaturePython — macro-defined, semantics opaque (R4)
  Placement = pos=(23981.4,19787,3350) rot=(0,0,1;0rad)
  Text = Corner 3 | 1.95
FEATURE [Part::FeaturePython] Punch001  # WARN: FeaturePython — macro-defined, semantics opaque (R4)
  Area = 1.55324e+06
  Av = 400
  Fys = 340000
  I22 = 3.0566e+11
  I23 = 0
  I33 = 2.64378e+11
  Location = 2
  Ratio = 1.95
  Use_Reinforcement = true
  Vc = 1.94155e+09
  Vs = 3.11166e+09
  Vu = 3.78991e+09
  alpha_s = 20
  angle = 0
  b0 = 2004.18
  bx = 550
  by = 550
  center_of_column = (23500,19838.5,0)
  center_of_load = (23500,19838.5,0)
  center_of_punch = (23158.8,19536.7,-387.5)
  column = -> Structure001
  combos_ratio = Combo1=1.33,Combo10=1.43,Combo11=1.49,Combo12=1.15,Combo13=1.09,Combo14=0.83,Combo15=0.78,Combo16=1.95,Combo17=1.88,Combo18=1.76,Combo19=1.68,+30 more (map truncated)
  d = 775
  fc = 25000
  foundation = -> Foundation
  gamma_vx = 0.4
  gamma_vy = 0.4
  id = C2_Story1
  one_way_shear_capacity = 9.70777e+08
  s = 33.8726
  text = -> Text001
  user_location = false
  vc = 1250
  x = 3348.35
FEATURE [App::FeaturePython] Text002  # WARN: FeaturePython — macro-defined, semantics opaque (R4)
  Placement = pos=(23889.7,15250,3350) rot=(0,0,1;0rad)
  Text = Edge 2 | 0.74
FEATURE [Part::FeaturePython] Punch002  # WARN: FeaturePython — macro-defined, semantics opaque (R4)
  Area = 2.32559e+06
  Av = 400
  Fys = 340000
  I22 = 8.36268e+11
  I23 = 2.44443e+11
  I33 = 4.52121e+11
  Location = 5
  Ratio = 0.74
  Use_Reinforcement = false
  Vc = 2.90698e+09
  Vs = 0
  Vu = 2.1628e+09
  alpha_s = 30
  angle = 0
  b0 = 3000.76
  bx = 600
  by = 600
  center_of_column = (23370,15250,0)
  center_of_load = (23370,15250,0)
  center_of_punch = (23141.3,15250,-387.5)
  column = -> Structure002
  combos_ratio = Combo1=0.64,Combo10=0.74,Combo11=0.71,Combo12=0.57,Combo13=0.56,Combo14=0.54,Combo15=0.53,Combo16=0.66,Combo17=0.64,Combo18=0.63,Combo19=0.62,+30 more (map truncated)
  d = 775
  fc = 25000
  foundation = -> Foundation
  gamma_vx = 0.4
  gamma_vy = 0.4
  id = C17_Story1
  one_way_shear_capacity = 1.45349e+09
  s = 0
  text = -> Text002
  user_location = false
  vc = 1250
  x = 0
FEATURE [App::FeaturePython] Text003  # WARN: FeaturePython — macro-defined, semantics opaque (R4)
  Placement = pos=(23768.5,10750,3350) rot=(0,0,1;0rad)
  Text = Edge 2 | 0.78
FEATURE [Part::FeaturePython] Punch003  # WARN: FeaturePython — macro-defined, semantics opaque (R4)
  Area = 2.32557e+06
  Av = 400
  Fys = 340000
  I22 = 8.36262e+11
  I23 = 2.44103e+11
  I33 = 4.51427e+11
  Location = 5
  Ratio = 0.78
  Use_Reinforcement = false
  Vc = 2.90697e+09
  Vs = 0
  Vu = 2.25581e+09
  alpha_s = 30
  angle = 0
  b0 = 3000.74
  bx = 600
  by = 600
  center_of_column = (23250,10750,0)
  center_of_load = (23250,10750,0)
  center_of_punch = (23020.6,10750,-387.5)
  column = -> Structure003
  combos_ratio = Combo1=0.65,Combo10=0.78,Combo11=0.76,Combo12=0.47,Combo13=0.46,Combo14=0.49,Combo15=0.49,Combo16=0.59,Combo17=0.58,Combo18=0.52,Combo19=0.51,+30 more (map truncated)
  d = 775
  fc = 25000
  foundation = -> Foundation
  gamma_vx = 0.4
  gamma_vy = 0.4
  id = C18_Story1
  one_way_shear_capacity = 1.45348e+09
  s = 0
  text = -> Text003
  user_location = false
  vc = 1250
  x = 0
FEATURE [App::FeaturePython] Text004  # WARN: FeaturePython — macro-defined, semantics opaque (R4)
  Placement = pos=(17740,4850,3350) rot=(0,0,1;0rad)
  Text = Edge 1 | 1.10
FEATURE [Part::FeaturePython] Punch004  # WARN: FeaturePython — macro-defined, semantics opaque (R4)
  Area = 2.325e+06
  Av = 400
  Fys = 340000
  I22 = 4.50953e+11
  I23 = 2.44206e+11
  I33 = 8.35991e+11
  Location = 4
  Ratio = 1.1
  Use_Reinforcement = true
  Vc = 2.90625e+09
  Vs = 1.34075e+09
  Vu = 3.18525e+09
  alpha_s = 30
  angle = 0
  b0 = 3000
  bx = 600
  by = 600
  center_of_column = (17740,5350,0)
  center_of_load = (17740,5350,0)
  center_of_punch = (17740,5579.17,-387.5)
  column = -> Structure004
  combos_ratio = Combo1=0.70,Combo10=0.99,Combo11=1.00,Combo12=0.52,Combo13=0.55,Combo14=0.62,Combo15=0.65,Combo16=0.42,Combo17=0.42,Combo18=0.44,Combo19=0.44,+30 more (map truncated)
  d = 775
  fc = 25000
  foundation = -> Foundation
  gamma_vx = 0.4
  gamma_vy = 0.4
  id = C5_Story1
  one_way_shear_capacity = 1.45312e+09
  s = 78.6127
  text = -> Text004
  user_location = false
  vc = 1250
  x = 1182.4
FEATURE [App::FeaturePython] Text005  # WARN: FeaturePython — macro-defined, semantics opaque (R4)
  Placement = pos=(12940,4850,3350) rot=(0,0,1;0rad)
  Text = Edge 1 | 1.40
FEATURE [Part::FeaturePython] Punch005  # WARN: FeaturePython — macro-defined, semantics opaque (R4)
  Area = 2.325e+06
  Av = 400
  Fys = 340000
  I22 = 4.50953e+11
  I23 = 2.44206e+11
  I33 = 8.35991e+11
  Location = 4
  Ratio = 1.4
  Use_Reinforcement = true
  Vc = 2.90625e+09
  Vs = 2.51875e+09
  Vu = 4.06875e+09
  alpha_s = 30
  angle = 0
  b0 = 3000
  bx = 600
  by = 600
  center_of_column = (12940,5350,0)
  center_of_load = (12940,5350,0)
  center_of_punch = (12940,5579.17,-387.5)
  column = -> Structure005
  combos_ratio = Combo1=1.09,Combo10=1.08,Combo11=1.07,Combo12=1.04,Combo13=1.09,Combo14=1.22,Combo15=1.23,Combo16=0.71,Combo17=0.72,Combo18=0.76,Combo19=0.79,+30 more (map truncated)
  d = 775
  fc = 25000
  foundation = -> Foundation
  gamma_vx = 0.4
  gamma_vy = 0.4
  id = C6_Story1
  one_way_shear_capacity = 1.45312e+09
  s = 41.8462
  text = -> Text005
  user_location = false
  vc = 1250
  x = 1617.85
FEATURE [App::FeaturePython] Text006  # WARN: FeaturePython — macro-defined, semantics opaque (R4)
  Placement = pos=(23618.6,5431.25,3350) rot=(0,0,1;0rad)
  Text = Corner 2 | 1.30
FEATURE [Part::FeaturePython] Punch006  # WARN: FeaturePython — macro-defined, semantics opaque (R4)
  Area = 1.5503e+06
  Av = 400
  Fys = 340000
  I22 = 2.73483e+11
  I23 = 0
  I33 = 2.83154e+11
  Location = 1
  Ratio = 1.3
  Use_Reinforcement = true
  Vc = 1.93787e+09
  Vs = 1.43144e+09
  Vu = 2.52699e+09
  alpha_s = 20
  angle = 0
  b0 = 2000.39
  bx = 550
  by = 550
  center_of_column = (23100,5350,0)
  center_of_load = (23100,5350,0)
  center_of_punch = (22778,5681.31,-387.5)
  column = -> Structure006
  combos_ratio = Combo1=0.80,Combo10=1.22,Combo11=1.20,Combo12=0.16,Combo13=0.18,Combo14=0.46,Combo15=0.48,Combo16=0.34,Combo17=0.34,Combo18=0.18,Combo19=0.13,+30 more (map truncated)
  d = 775
  fc = 25000
  foundation = -> Foundation
  gamma_vx = 0.4
  gamma_vy = 0.4
  id = C19_Story1
  one_way_shear_capacity = 9.68937e+08
  s = 73.632
  text = -> Text006
  user_location = false
  vc = 1250
  x = 2103.44
FEATURE [App::FeaturePython] Text007  # WARN: FeaturePython — macro-defined, semantics opaque (R4)
  Placement = pos=(11240,21445.8,3350) rot=(0,0,1;0rad)
  Text = Edge 3 | 1.74
FEATURE [Part::FeaturePython] Punch007  # WARN: FeaturePython — macro-defined, semantics opaque (R4)
  Area = 2.34819e+06
  Av = 400
  Fys = 340000
  I22 = 4.60028e+11
  I23 = 2.87438e+11
  I33 = 8.55594e+11
  Location = 6
  Ratio = 1.74
  Use_Reinforcement = true
  Vc = 2.93523e+09
  Vs = 3.89016e+09
  Vu = 5.11905e+09
  alpha_s = 30
  angle = 0
  b0 = 3029.92
  bx = 600
  by = 600
  center_of_column = (11240,20890,0)
  center_of_load = (11240,20890,0)
  center_of_punch = (11290.5,20656.5,-387.5)
  column = -> Structure007
  combos_ratio = Combo1=1.39,Combo10=1.42,Combo11=1.38,Combo12=1.50,Combo13=1.50,Combo14=1.30,Combo15=1.30,Combo16=1.74,Combo17=1.74,Combo18=1.74,Combo19=1.74,+30 more (map truncated)
  d = 775
  fc = 25000
  foundation = -> Foundation
  gamma_vx = 0.4
  gamma_vy = 0.4
  id = C8_Story1
  one_way_shear_capacity = 1.46762e+09
  s = 27.094
  text = -> Text007
  user_location = false
  vc = 1250
  x = 2135.51
FEATURE [App::FeaturePython] Text008  # WARN: FeaturePython — macro-defined, semantics opaque (R4)
  Placement = pos=(6930,21675.3,3350) rot=(0,0,1;0rad)
  Text = Edge 3 | 2.43
FEATURE [Part::FeaturePython] Punch008  # WARN: FeaturePython — macro-defined, semantics opaque (R4)
  Area = 1.87204e+06
  Av = 400
  Fys = 340000
  I22 = 2.936e+11
  I23 = 2.31599e+11
  I33 = 8.04502e+11
  Location = 6
  Ratio = 2.43
  Use_Reinforcement = true
  Vc = 2.34005e+09
  Vs = 5.24794e+09
  Vu = 5.69099e+09
  Warnings = Vs > 2 * Vc
  alpha_s = 30
  angle = 0
  b0 = 2415.53
  bx = 650
  by = 650
  center_of_column = (6930,21230,0)
  center_of_load = (6930,21230,0)
  center_of_punch = (6902.36,20903.9,-387.5)
  column = -> Structure008
  combos_ratio = Combo1=1.67,Combo10=1.32,Combo11=1.27,Combo12=2.24,Combo13=2.26,Combo14=1.86,Combo15=1.86,Combo16=2.18,Combo17=2.20,Combo18=2.42,Combo19=2.43,+30 more (map truncated)
  d = 775
  fc = 25000
  foundation = -> Foundation
  gamma_vx = 0.4
  gamma_vy = 0.4
  id = C9_Story1
  one_way_shear_capacity = 1.17002e+09
  s = 20.0841
  text = -> Text008
  user_location = false
  vc = 1250
  x = 2417.4
FEATURE [App::FeaturePython] Text009  # WARN: FeaturePython — macro-defined, semantics opaque (R4)
  Placement = pos=(2400,17580,3350) rot=(0,0,1;0rad)
  Text = Edge 4 | 2.11
FEATURE [Part::FeaturePython] Punch009  # WARN: FeaturePython — macro-defined, semantics opaque (R4)
  Area = 2.56381e+06
  Av = 400
  Fys = 340000
  I22 = 9.48133e+11
  I23 = 2.3381e+11
  I33 = 3.9558e+11
  Location = 7
  Ratio = 2.11
  Use_Reinforcement = true
  Vc = 3.20477e+09
  Vs = 5.81986e+09
  Vu = 6.76847e+09
  alpha_s = 30
  angle = 0
  b0 = 3308.15
  bx = 650
  by = 650
  center_of_column = (2900,17580,0)
  center_of_load = (2900,17580,0)
  center_of_punch = (3322.32,17463.3,-387.5)
  column = -> Structure009
  combos_ratio = Combo1=1.83,Combo10=1.55,Combo11=1.57,Combo12=2.10,Combo13=2.08,Combo14=2.11,Combo15=2.10,Combo16=1.74,Combo17=1.72,Combo18=1.90,Combo19=1.88,+30 more (map truncated)
  d = 775
  fc = 25000
  foundation = -> Foundation
  gamma_vx = 0.4
  gamma_vy = 0.4
  id = C10_Story1
  one_way_shear_capacity = 1.60238e+09
  s = 18.1104
  text = -> Text009
  user_location = false
  vc = 1250
  x = 2948.45
FEATURE [App::FeaturePython] Text010  # WARN: FeaturePython — macro-defined, semantics opaque (R4)
  Placement = pos=(2400,5456.25,3350) rot=(0,0,1;0rad)
  Text = Corner 1 | 2.79
FEATURE [Part::FeaturePython] Punch010  # WARN: FeaturePython — macro-defined, semantics opaque (R4)
  Area = 1.55e+06
  Av = 400
  Fys = 340000
  I22 = 3.0009e+11
  I23 = 0
  I33 = 3.0009e+11
  Location = 0
  Ratio = 2.79
  Use_Reinforcement = true
  Vc = 1.9375e+09
  Vs = 5.27517e+09
  Vu = 5.4095e+09
  Warnings = Vs > 2 * Vc
  alpha_s = 20
  angle = 0
  b0 = 2000
  bx = 650
  by = 650
  center_of_column = (2900,5350,0)
  center_of_load = (2900,5350,0)
  center_of_punch = (3256.25,5706.25,-387.5)
  column = -> Structure010
  combos_ratio = Combo1=1.68,Combo10=1.93,Combo11=2.08,Combo12=1.29,Combo13=1.14,Combo14=1.93,Combo15=1.78,Combo16=0.66,Combo17=0.54,Combo18=0.62,Combo19=0.67,+30 more (map truncated)
  d = 775
  fc = 25000
  foundation = -> Foundation
  gamma_vx = 0.4
  gamma_vy = 0.4
  id = C16_Story1
  one_way_shear_capacity = 9.6875e+08
  s = 19.9804
  text = -> Text010
  user_location = false
  vc = 1250
  x = 4944.83
FEATURE [App::FeaturePython] Text011  # WARN: FeaturePython — macro-defined, semantics opaque (R4)
  Placement = pos=(17740,11437.5,3350) rot=(0,0,1;0rad)
  Text = Interior | 0.77
FEATURE [Part::FeaturePython] Punch011  # WARN: FeaturePython — macro-defined, semantics opaque (R4)
  Area = 3.1e+06
  Av = 400
  Fys = 340000
  I22 = 9.39365e+11
  I23 = 0
  I33 = 9.39365e+11
  Location = 8
  Ratio = 0.77
  Use_Reinforcement = false
  Vc = 3.875e+09
  Vs = 0
  Vu = 2.976e+09
  alpha_s = 40
  angle = 0
  b0 = 4000
  bx = 600
  by = 600
  center_of_column = (17740,10750,0)
  center_of_load = (17740,10750,0)
  center_of_punch = (17740,10750,-387.5)
  column = -> Structure011
  combos_ratio = Combo1=0.62,Combo10=0.74,Combo11=0.74,Combo12=0.64,Combo13=0.64,Combo14=0.67,Combo15=0.68,Combo16=0.63,Combo17=0.62,Combo18=0.62,Combo19=0.62,+30 more (map truncated)
  d = 775
  fc = 25000
  foundation = -> Foundation
  gamma_vx = 0.4
  gamma_vy = 0.4
  id = C12_Story1
  one_way_shear_capacity = 1.9375e+09
  s = 0
  text = -> Text011
  user_location = false
  vc = 1250
  x = 0
FEATURE [App::FeaturePython] Text012  # WARN: FeaturePython — macro-defined, semantics opaque (R4)
  Placement = pos=(17240,15250,3350) rot=(0,0,1;0rad)
  Text = Edge 4 | 1.18
FEATURE [Part::FeaturePython] Punch012  # WARN: FeaturePython — macro-defined, semantics opaque (R4)
  Area = 2.325e+06
  Av = 400
  Fys = 340000
  I22 = 7.83678e+11
  I23 = 2.26768e+11
  I33 = 4.33516e+11
  Location = 7
  Ratio = 1.18
  Use_Reinforcement = true
  Vc = 2.90625e+09
  Vs = 1.68175e+09
  Vu = 3.441e+09
  alpha_s = 30
  angle = 0
  b0 = 3000
  bx = 550
  by = 550
  center_of_column = (17740,15250,0)
  center_of_load = (17740,15250,0)
  center_of_punch = (17960.8,15250,-387.5)
  column = -> Structure012
  combos_ratio = Combo1=1.10,Combo10=1.06,Combo11=1.06,Combo12=1.02,Combo13=1.02,Combo14=0.99,Combo15=0.99,Combo16=1.11,Combo17=1.11,Combo18=1.10,Combo19=1.10,+30 more (map truncated)
  d = 775
  fc = 25000
  foundation = -> Foundation
  gamma_vx = 0.4
  gamma_vy = 0.4
  id = C13_Story1
  one_way_shear_capacity = 1.45312e+09
  s = 62.6728
  text = -> Text012
  user_location = false
  vc = 1250
  x = 1308.46
FEATURE [App::FeaturePython] Text013  # WARN: FeaturePython — macro-defined, semantics opaque (R4)
  Placement = pos=(12940,11387.5,3350) rot=(0,0,1;1.5708rad)
  Text = Interior | 1.02
FEATURE [Part::FeaturePython] Punch013  # WARN: FeaturePython — macro-defined, semantics opaque (R4)
  Area = 3.1e+06
  Av = 400
  Fys = 340000
  I22 = 8.36677e+11
  I23 = 0.00179739
  I33 = 8.36677e+11
  Location = 8
  Ratio = 1.02
  Use_Reinforcement = true
  Vc = 3.875e+09
  Vs = 1.37433e+09
  Vu = 3.937e+09
  alpha_s = 40
  angle = 90
  b0 = 4000
  bx = 500
  by = 500
  center_of_column = (12940,10750,0)
  center_of_load = (12940,10750,0)
  center_of_punch = (12940,10750,-387.5)
  column = -> Structure013
  combos_ratio = Combo1=0.69,Combo10=0.72,Combo11=0.71,Combo12=0.74,Combo13=0.75,Combo14=0.88,Combo15=0.89,Combo16=0.47,Combo17=0.48,Combo18=0.54,Combo19=0.55,+30 more (map truncated)
  d = 775
  fc = 25000
  foundation = -> Foundation
  gamma_vx = 0.4
  gamma_vy = 0.4
  id = C14_Story1
  one_way_shear_capacity = 1.9375e+09
  s = 76.6917
  text = -> Text013
  user_location = false
  vc = 1250
  x = 582.709
FEATURE [App::FeaturePython] Text014  # WARN: FeaturePython — macro-defined, semantics opaque (R4)
  Placement = pos=(12940,13687.5,3350) rot=(0,0,1;1.5708rad)
  Text = Interior | 1.08
FEATURE [Part::FeaturePython] Punch014  # WARN: FeaturePython — macro-defined, semantics opaque (R4)
  Area = 3.0297e+06
  Av = 400
  Fys = 340000
  I22 = 8.19958e+11
  I23 = 1.47135e+11
  I33 = 8.36951e+11
  Location = 8
  Ratio = 1.08
  Use_Reinforcement = true
  Vc = 3.78712e+09
  Vs = 1.66633e+09
  Vu = 4.09009e+09
  alpha_s = 40
  angle = 90
  b0 = 3909.29
  bx = 500
  by = 500
  center_of_column = (12940,13050,0)
  center_of_load = (12940,13050,0)
  center_of_punch = (12985,13067.6,-387.5)
  column = -> Structure014
  combos_ratio = Combo1=0.90,Combo10=0.83,Combo11=0.83,Combo12=0.97,Combo13=0.97,Combo14=0.87,Combo15=0.87,Combo16=1.08,Combo17=1.08,Combo18=1.08,Combo19=1.08,+30 more (map truncated)
  d = 775
  fc = 25000
  foundation = -> Foundation
  gamma_vx = 0.4
  gamma_vy = 0.4
  id = C15_Story1
  one_way_shear_capacity = 1.89356e+09
  s = 63.2526
  text = -> Text014
  user_location = false
  vc = 1250
  x = 620.436
FEATURE [App::FeaturePython] Text015  # WARN: FeaturePython — macro-defined, semantics opaque (R4)
  Placement = pos=(2400,10750,3350) rot=(0,0,1;0rad)
  Text = Edge 4 | 1.55
FEATURE [Part::FeaturePython] Punch015  # WARN: FeaturePython — macro-defined, semantics opaque (R4)
  Area = 2.325e+06
  Av = 400
  Fys = 340000
  I22 = 8.90241e+11
  I23 = 2.62289e+11
  I33 = 4.69036e+11
  Location = 7
  Ratio = 1.55
  Use_Reinforcement = true
  Vc = 2.90625e+09
  Vs = 3.10775e+09
  Vu = 4.5105e+09
  alpha_s = 30
  angle = 0
  b0 = 3000
  bx = 650
  by = 650
  center_of_column = (2900,10750,0)
  center_of_load = (2900,10750,0)
  center_of_punch = (3137.5,10750,-387.5)
  column = -> Structure015
  combos_ratio = Combo1=1.42,Combo10=1.50,Combo11=1.51,Combo12=1.30,Combo13=1.30,Combo14=1.28,Combo15=1.26,Combo16=1.48,Combo17=1.48,Combo18=1.41,Combo19=1.41,+30 more (map truncated)
  d = 775
  fc = 25000
  foundation = -> Foundation
  gamma_vx = 0.4
  gamma_vy = 0.4
  id = C11_Story1
  one_way_shear_capacity = 1.45312e+09
  s = 33.9152
  text = -> Text015
  user_location = false
  vc = 1250
  x = 1835.58
FEATURE [App::DocumentObjectGroup] Punches
  Group = -> [Punch,Punch001,Punch002,Punch003,Punch004,Punch005,Punch006,Punch007,Punch008,Punch009,Punch010,Punch011,Punch012,Punch013,Punch014,Punch015]
FEATURE [Part::FeaturePython] SingleFoundation  # Arch/BIM 77 (typed FeaturePython)
  Bx = 8000
  By = 8000
  HorizontalArea = 0
  IfcData = attributes={"GlobalId": {"name": "GlobalId", "type": "IfcGloballyUniqueId", "is_enum": false, "enum_values": []}, "Description": {"... (+511 chars omitted),+1 more (map truncated)
  IfcType = 77
  MoveBase = false
  MoveWithHost = false
  PerimeterLength = 0
  Placement = pos=(27967.6,16168.5,-1100) rot=(0,0,1;0rad)
  PredefinedType = 0
  VerticalArea = 0
  angle = 0
  design_layer_a = true
  design_layer_b = true
  design_type = 0
  fc = 25000
  ks = 2
  no_of_design_layer_a = 1
  no_of_design_layer_b = 1
  thickness = 1100
FEATURE [Part::FeaturePython] SingleFoundation001  # Arch/BIM 77 (typed FeaturePython)
  Bx = 8000
  By = 8000
  HorizontalArea = 0
  IfcData = attributes={"GlobalId": {"name": "GlobalId", "type": "IfcGloballyUniqueId", "is_enum": false, "enum_values": []}, "Description": {"... (+511 chars omitted),+1 more (map truncated)
  IfcType = 77
  MoveBase = false
  MoveWithHost = false
  PerimeterLength = 0
  Placement = pos=(33320.3,5629.06,-1550) rot=(0,0,1;0rad)
  PredefinedType = 0
  VerticalArea = 0
  angle = 0
  design_layer_a = true
  design_layer_b = true
  design_type = 0
  fc = 25000
  ks = 2
  no_of_design_layer_a = 1
  no_of_design_layer_b = 1
  thickness = 1550
note: 2 file-system paths scrubbed to <path> (originals preserved in the JSON sidecar)
